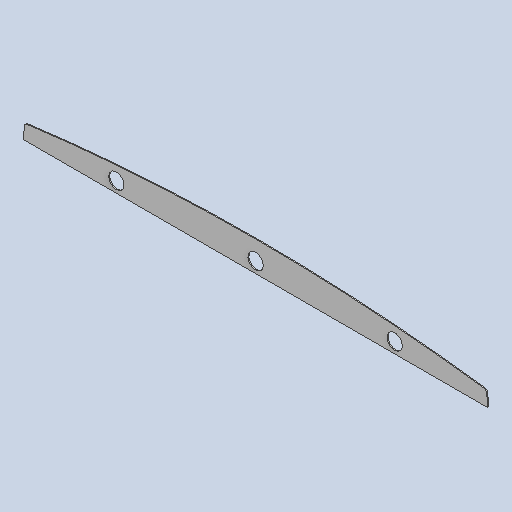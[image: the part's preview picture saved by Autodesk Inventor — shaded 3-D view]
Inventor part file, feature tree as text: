
AUTODESK INVENTOR PART (.ipt)
format: ipt  version: 2025 (Build 290162010, 162A)  size: 208,384 bytes
history: native  units: mm
features: other x3, sheet_metal_op x1, mirror x1, sketch x1
ambient origin geometry x8: Origin, YZ Plane, XZ Plane, XY Plane, X Axis, Y Axis, Z Axis, Center Point
bodies: Body1 (feature_tree)
feature tree (6):
  sheet_metal_op  "Face1"
  mirror  "Mirror3"
  other  "Corner Chamfer2"
  sketch  "Sketch1"  dims[d54=1500.0mm d55=2700.0mm d58=2100.0mm d65=6.0mm d66=6.0mm d68=6.0mm d69=3.0mm d70=3.0mm d75=3.0mm d78=3.0mm d80=3.0mm d83=6.0mm d86=3.0mm d112=251.771mm d113=50.0mm d114=50.0mm d115=3.0mm d117=110.0mm d118=25.0mm d119=122.6mm d120=25.0mm d121=50.0mm d122=50.0mm d123=450.0mm d124=35.0mm d125=3.0mm d126=98.5mm d127=5.0mm d128=5.0mm d132=0.2mm d133=0.2mm d134=2.0mm d135=6.0mm d136=45.0deg]
  other  "Plate3"
  other  "Definition1"
